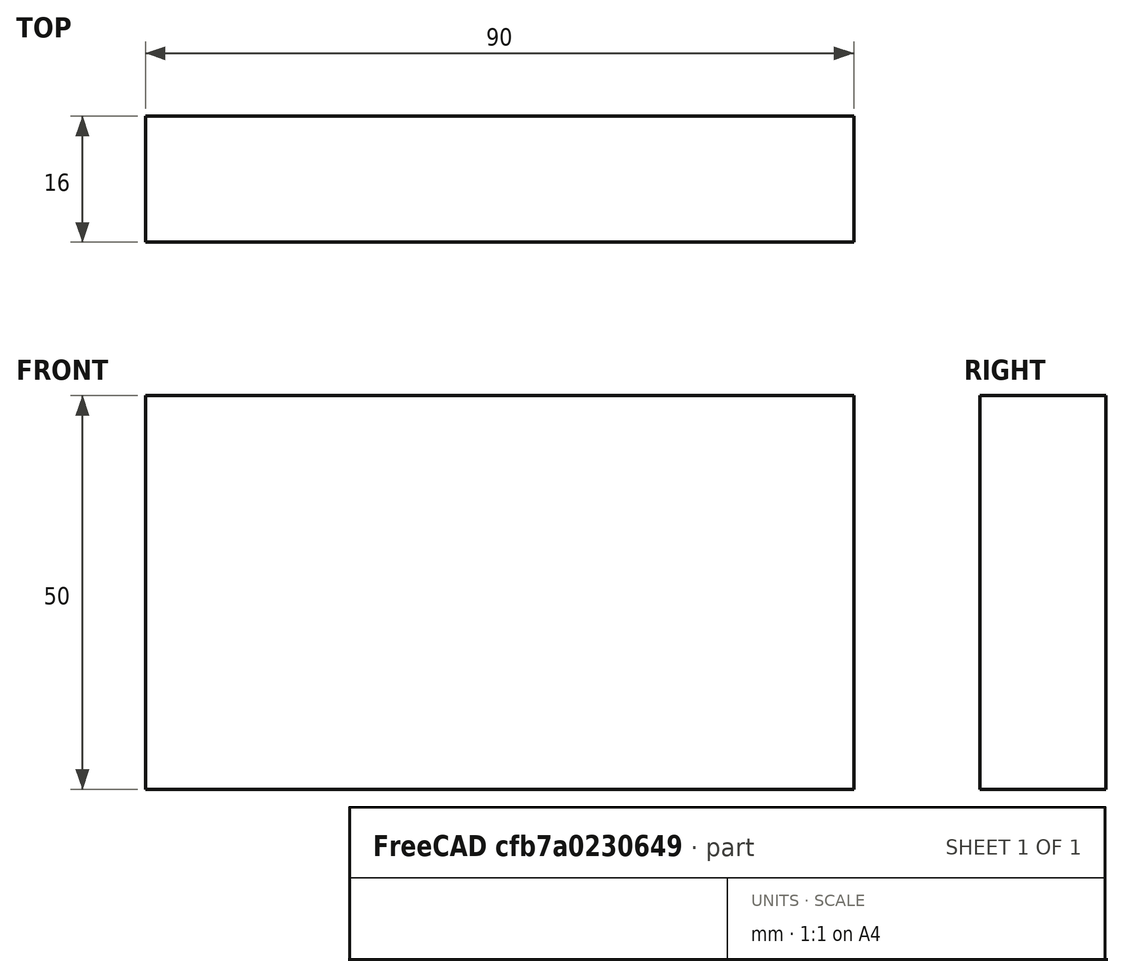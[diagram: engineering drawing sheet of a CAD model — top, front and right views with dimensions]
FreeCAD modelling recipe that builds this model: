
FCSTD DOCUMENT  (FreeCAD 0.15R4671 (Git))
Label: Flat Bar 90x16 EN10058 S235JR
License: All rights reserved
LicenseURL: http://en.wikipedia.org/wiki/All_rights_reserved
objects: Sketcher::SketchObject×1, Part::Extrusion×1
note: 2 computed .brp shape members not serialized (recipe doc carries the construction recipe); baked Part::Feature solids carry a one-line shape summary decoded from their .brp

FEATURE [Sketcher::SketchObject] Sketch
  sketch-geometry (4):
    g0: LineSegment StartX=-45 StartY=-8 StartZ=0 EndX=45 EndY=-8 EndZ=0
    g1: LineSegment StartX=45 StartY=-8 StartZ=0 EndX=45 EndY=8 EndZ=0
    g2: LineSegment StartX=45 StartY=8 StartZ=0 EndX=-45 EndY=8 EndZ=0
    g3: LineSegment StartX=-45 StartY=8 StartZ=0 EndX=-45 EndY=-8 EndZ=0
  constraints (12):
    c: Coincident(g0,g1)
    c: Coincident(g1,g2)
    c: Coincident(g2,g3)
    c: Coincident(g3,g0)
    c: Horizontal(g0)
    c: Horizontal(g2)
    c: Vertical(g1)
    c: Vertical(g3)
    c: Symmetric(g1,g2,g-2)
    c: Symmetric(g0,g1,g-1)
    c: DistanceY(g1) = 16
    c: DistanceX(g0) = 90
FEATURE [Part::Extrusion] Extrude  label="Flat Bar 90x16 EN10058 S235JR"
  Base = -> Sketch
  Dir = (0,0,50)
  Solid = true
